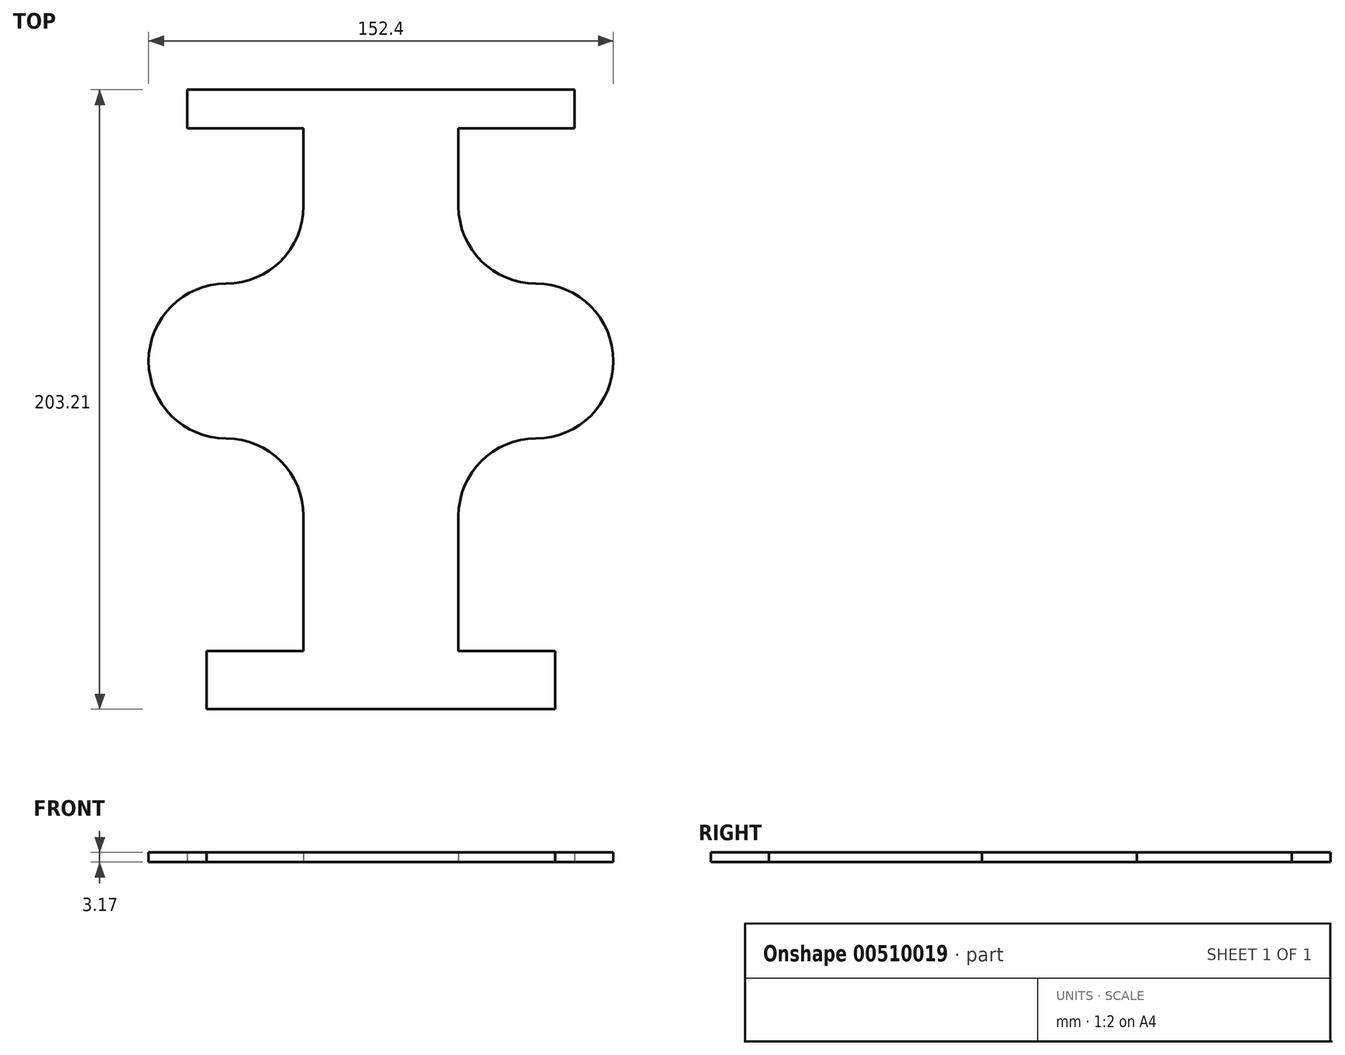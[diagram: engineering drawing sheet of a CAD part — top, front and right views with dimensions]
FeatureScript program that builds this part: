
annotation { "Feature Type Name" : "Feature", "Feature Type Description" : "" }
export const myFeature = defineFeature(function(context is Context, id is Id, definition is map)
    precondition{}
    {
        {
            var Q0;
            Q0=qCreatedBy(makeId("Top.planeOp"),FACE);
            var sketch = newSketch(context, id + "F0", { "sketchPlane" : qUnion([Q0])});
            skLineSegment(sketch, "E0.left", {"start": v(-25.4, 9.52) * mm, "end": v(-25.4, 53.87) * mm});
            skLineSegment(sketch, "E0.right", {"start": v(25.4, 9.52) * mm, "end": v(25.4, 53.87) * mm});
            skLineSegment(sketch, "E1.bottom", {"start": v(63.5, 193.68) * mm, "end": v(-63.5, 193.68) * mm});
            skLineSegment(sketch, "E1.top", {"start": v(63.5, 180.98) * mm, "end": v(25.4, 180.98) * mm});
            skLineSegment(sketch, "E1.left", {"start": v(63.5, 193.68) * mm, "end": v(63.5, 180.98) * mm});
            skLineSegment(sketch, "E1.right", {"start": v(-63.5, 193.68) * mm, "end": v(-63.5, 180.98) * mm});
            skPoint(sketch, "E1.middle", {"position": v(0, 187.33) * mm});
            skLineSegment(sketch, "E2.bottom", {"start": v(57.15, -9.53) * mm, "end": v(-57.15, -9.53) * mm});
            skLineSegment(sketch, "E2.top", {"start": v(57.15, 9.52) * mm, "end": v(25.4, 9.52) * mm});
            skLineSegment(sketch, "E2.left", {"start": v(57.15, -9.53) * mm, "end": v(57.15, 9.52) * mm});
            skLineSegment(sketch, "E2.right", {"start": v(-57.15, -9.53) * mm, "end": v(-57.15, 9.52) * mm});
            skPoint(sketch, "E2.middle", {"position": v(0, 0) * mm});
            skLineSegment(sketch, "E3.bottom", {"start": v(50.8, 130.07) * mm, "end": v(50.8, 130.07) * mm});
            skLineSegment(sketch, "E3.left", {"start": v(76.2, 104.85) * mm, "end": v(76.2, 104.85) * mm});
            skLineSegment(sketch, "E3.right", {"start": v(-76.2, 104.48) * mm, "end": v(-76.2, 104.48) * mm});
            skLineSegment(sketch, "E4.trimOffspring", {"start": v(-25.4, 180.98) * mm, "end": v(-63.5, 180.98) * mm});
            skLineSegment(sketch, "E5.trimOffspring", {"start": v(-50.8, 130.07) * mm, "end": v(-50.8, 130.07) * mm});
            skLineSegment(sketch, "E6.trimOffspring", {"start": v(-50.8, 79.27) * mm, "end": v(-50.8, 79.27) * mm});
            skLineSegment(sketch, "E7.trimOffspring", {"start": v(-25.4, 155.47) * mm, "end": v(-25.4, 180.98) * mm});
            skLineSegment(sketch, "E8.trimOffspring", {"start": v(-25.4, 9.52) * mm, "end": v(-57.15, 9.52) * mm});
            skPoint(sketch, "E9.orphan", {"position": v(-25.4, 0) * mm});
            skPoint(sketch, "E10.orphan", {"position": v(25.4, 0) * mm});
            skPoint(sketch, "E11.orphan", {"position": v(25.4, 187.33) * mm});
            skPoint(sketch, "E12.orphan", {"position": v(-25.4, 187.32) * mm});
            skLineSegment(sketch, "E13", {"start": v(50.8, 79.27) * mm, "end": v(50.8, 79.27) * mm});
            skLineSegment(sketch, "E14.trimOffspring", {"start": v(25.4, 155.47) * mm, "end": v(25.4, 180.98) * mm});
            skPoint(sketch, "E15.visualSharp", {"position": v(-25.4, 130.07) * mm});
            skArc(sketch, "E15.filletArc", {"start": v(-50.8, 130.07) * mm, "mid": v(-32.84, 137.5) * mm, "end": v(-25.4, 155.47) * mm});
            skPoint(sketch, "E16.visualSharp", {"position": v(-76.39, 130.07) * mm});
            skArc(sketch, "E16.filletArc", {"start": v(-50.8, 130.07) * mm, "mid": v(-68.83, 122.56) * mm, "end": v(-76.2, 104.48) * mm});
            skPoint(sketch, "E17.visualSharp", {"position": v(-76.02, 79.27) * mm});
            skArc(sketch, "E17.filletArc", {"start": v(-76.2, 104.48) * mm, "mid": v(-68.7, 86.64) * mm, "end": v(-50.8, 79.27) * mm});
            skPoint(sketch, "E18.visualSharp", {"position": v(76.39, 79.27) * mm});
            skArc(sketch, "E18.filletArc", {"start": v(50.8, 79.27) * mm, "mid": v(68.83, 86.77) * mm, "end": v(76.2, 104.85) * mm});
            skPoint(sketch, "E19.visualSharp", {"position": v(76.02, 130.07) * mm});
            skArc(sketch, "E19.filletArc", {"start": v(76.2, 104.85) * mm, "mid": v(68.7, 122.7) * mm, "end": v(50.8, 130.07) * mm});
            skPoint(sketch, "E20.visualSharp", {"position": v(25.4, 130.07) * mm});
            skArc(sketch, "E20.filletArc", {"start": v(25.4, 155.47) * mm, "mid": v(32.84, 137.5) * mm, "end": v(50.8, 130.07) * mm});
            skPoint(sketch, "E21.visualSharp", {"position": v(25.4, 79.27) * mm});
            skArc(sketch, "E21.filletArc", {"start": v(50.8, 79.27) * mm, "mid": v(32.84, 71.83) * mm, "end": v(25.4, 53.87) * mm});
            skPoint(sketch, "E22.visualSharp", {"position": v(-25.4, 79.27) * mm});
            skArc(sketch, "E22.filletArc", {"start": v(-25.4, 53.87) * mm, "mid": v(-32.84, 71.83) * mm, "end": v(-50.8, 79.27) * mm});
            skSolve(sketch);
        }
        {
            var Q0;
            Q0 = qSketchRegion(id + "F0", true);
            extrude(context, id + "F1", {"entities" : qUnion([Q0]), "depth" : 3.17 * mm, "offsetDistance" : 25.4 * mm});
        }
    });
